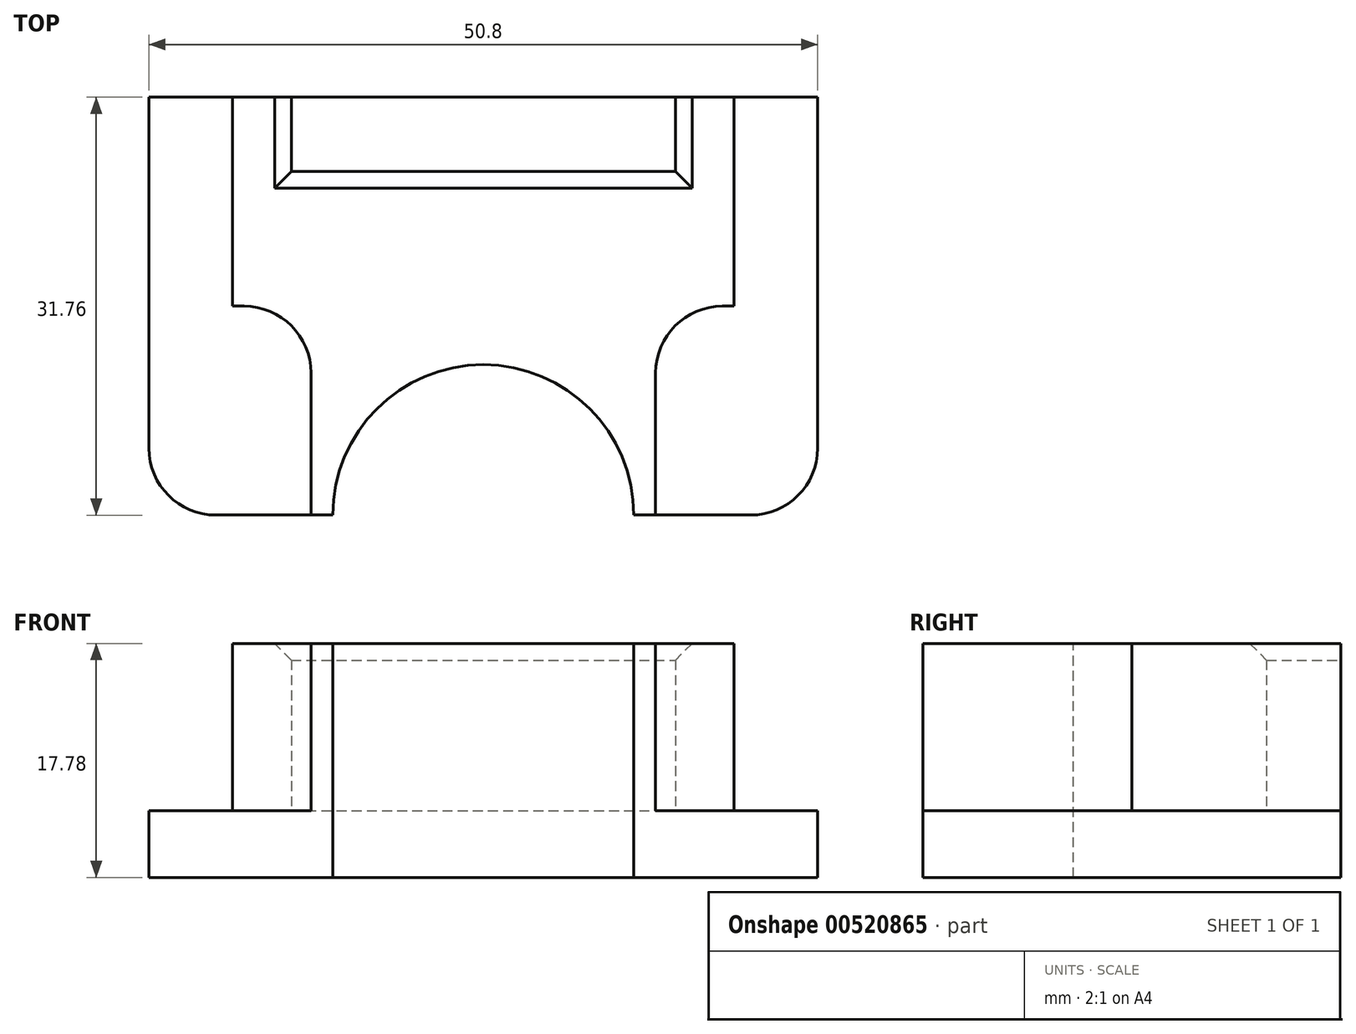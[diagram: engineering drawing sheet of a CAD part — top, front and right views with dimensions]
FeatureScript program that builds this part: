
annotation { "Feature Type Name" : "Feature", "Feature Type Description" : "" }
export const myFeature = defineFeature(function(context is Context, id is Id, definition is map)
    precondition{}
    {
        {
            var Q0;
            Q0=qCreatedBy(makeId("Top.planeOp"),FACE);
            var sketch = newSketch(context, id + "F0", { "sketchPlane" : qUnion([Q0])});
            skLineSegment(sketch, "E0.bottom", {"start": v(-25.4, 15.87) * mm, "end": v(25.4, 15.87) * mm});
            skLineSegment(sketch, "E0.top", {"start": v(-25.4, -15.88) * mm, "end": v(25.4, -15.88) * mm});
            skLineSegment(sketch, "E0.left", {"start": v(-25.4, 15.87) * mm, "end": v(-25.4, -15.88) * mm});
            skLineSegment(sketch, "E0.right", {"start": v(25.4, 15.87) * mm, "end": v(25.4, -15.88) * mm});
            skPoint(sketch, "E0.middle", {"position": v(0, 0) * mm});
            skSolve(sketch);
        }
        {
            var Q0;
            Q0=makeQuery(id+"F0.imprint","IMPRINT",FACE,{"disambiguationData":[TD([[makeQuery(id+"F0.imprint","IMPRINT",EDGE,{"derivedFrom":sQuery(id+"F0.wireOp",EDGE,"E0.bottom")}),-1.0]])]});
            extrude(context, id + "F1", {"entities" : qUnion([Q0]), "depth" : 5.08 * mm, "offsetDistance" : 25.4 * mm});
        }
        {
            var Q0;
            Q0=makeQuery(id+"F1.opExtrude","CAP_FACE",FACE,{"disambiguationData":[OSD([sQuery(id+"F0.wireOp",EDGE,"E0.bottom"),sQuery(id+"F0.wireOp",EDGE,"E0.top"),sQuery(id+"F0.wireOp",EDGE,"E0.left"),sQuery(id+"F0.wireOp",EDGE,"E0.right")])],"isStart":false});
            var sketch = newSketch(context, id + "F2", { "sketchPlane" : qUnion([Q0])});
            skLineSegment(sketch, "E1", {"start": v(-19.05, 15.87) * mm, "end": v(-19.05, 0) * mm});
            skLineSegment(sketch, "E2", {"start": v(-19.05, 0) * mm, "end": v(-13.1, 0) * mm});
            skLineSegment(sketch, "E3", {"start": v(-13.1, 0) * mm, "end": v(-13.1, -15.88) * mm});
            skLineSegment(sketch, "E4", {"start": v(-13.1, -15.88) * mm, "end": v(13.1, -15.88) * mm});
            skLineSegment(sketch, "E5", {"start": v(13.1, -15.88) * mm, "end": v(13.1, 0) * mm});
            skLineSegment(sketch, "E6", {"start": v(13.1, 0) * mm, "end": v(19.05, 0) * mm});
            skLineSegment(sketch, "E7", {"start": v(19.05, 0) * mm, "end": v(19.05, 15.87) * mm});
            skLineSegment(sketch, "E8", {"start": v(-19.05, 15.87) * mm, "end": v(-14.6, 15.87) * mm});
            skLineSegment(sketch, "E9", {"start": v(-14.6, 15.87) * mm, "end": v(-14.6, 10.23) * mm});
            skLineSegment(sketch, "E10", {"start": v(-14.6, 10.23) * mm, "end": v(14.6, 10.23) * mm});
            skLineSegment(sketch, "E11", {"start": v(14.6, 10.23) * mm, "end": v(14.6, 15.87) * mm});
            skLineSegment(sketch, "E12", {"start": v(14.6, 15.87) * mm, "end": v(19.05, 15.87) * mm});
            skLineSegment(sketch, "E13", {"start": v(0, 15.87) * mm, "end": v(0, -15.88) * mm, "construction": true});
            skSolve(sketch);
        }
        {
            var Q0;
            Q0=makeQuery(id+"F2.imprint","IMPRINT",FACE,{"disambiguationData":[TD([[makeQuery(id+"F2.imprint","IMPRINT",EDGE,{"derivedFrom":sQuery(id+"F2.wireOp",EDGE,"E1")}),1.0]])]});
            extrude(context, id + "F3", {"entities" : qUnion([Q0]), "operationType" : NewBodyOperationType.ADD, "depth" : 12.7 * mm, "offsetDistance" : 25.4 * mm});
        }
        {
            var Q0;
            Q0=makeQuery(id+"F3.opExtrude","CAP_FACE",FACE,{"disambiguationData":[OSD([sQuery(id+"F2.wireOp",EDGE,"E1"),sQuery(id+"F2.wireOp",EDGE,"E2"),sQuery(id+"F2.wireOp",EDGE,"E3"),sQuery(id+"F2.wireOp",EDGE,"E4"),sQuery(id+"F2.wireOp",EDGE,"E5"),sQuery(id+"F2.wireOp",EDGE,"E6"),sQuery(id+"F2.wireOp",EDGE,"E7"),sQuery(id+"F2.wireOp",EDGE,"E8"),sQuery(id+"F2.wireOp",EDGE,"E9"),sQuery(id+"F2.wireOp",EDGE,"E10"),sQuery(id+"F2.wireOp",EDGE,"E11"),sQuery(id+"F2.wireOp",EDGE,"E12")])],"isStart":false});
            var sketch = newSketch(context, id + "F4", { "sketchPlane" : qUnion([Q0])});
            skCircle(sketch, "E14", {"center": v(0, -15.88) * mm, "radius": 11.43 * mm});
            skSolve(sketch);
        }
        {
            var Q0;
            {var subQ0=sQuery(id+"F4.wireOp",EDGE,"E14");var subQ1=makeQuery(id+"F3.opExtrude","CAP_EDGE",EDGE,{"disambiguationData":[OSD([sQuery(id+"F2.wireOp",EDGE,"E4")])],"isStart":false});var subQ2=makeQuery(id+"F4.imprint","INTERSECT",VERTEX,{"disambiguationData":[OD(0.0)],"derivedFrom":[subQ1,subQ0]});Q0=makeQuery(id+"F4.imprint","IMPRINT",FACE,{"disambiguationData":[TD([[makeQuery(id+"F4.imprint","IMPRINT",EDGE,{"disambiguationData":[TD([[subQ2,1.0]])],"derivedFrom":subQ0}),1.0]])]});}
            var Q1;
            Q1=makeQuery(id+"F1.opExtrude","CAP_FACE",FACE,{"disambiguationData":[OSD([sQuery(id+"F0.wireOp",EDGE,"E0.bottom"),sQuery(id+"F0.wireOp",EDGE,"E0.top"),sQuery(id+"F0.wireOp",EDGE,"E0.left"),sQuery(id+"F0.wireOp",EDGE,"E0.right")])],"isStart":true});
            extrude(context, id + "F5", {"entities" : qUnion([Q0]), "operationType" : NewBodyOperationType.REMOVE, "endBound" : BoundingType.UP_TO_SURFACE, "oppositeDirection" : true, "depth" : 25.4 * mm, "endBoundEntityFace" : qUnion([Q1]), "offsetDistance" : 25.4 * mm});
        }
        {
            var Q0;
            Q0=makeQuery(id+"F3.opExtrude","SWEPT_EDGE",EDGE,{"disambiguationData":[OSD([sQuery(id+"F2.wireOp",EDGE,"E2"),sQuery(id+"F2.wireOp",EDGE,"E3")])]});
            var Q1;
            Q1=makeQuery(id+"F3.opExtrude","SWEPT_EDGE",EDGE,{"disambiguationData":[OSD([sQuery(id+"F2.wireOp",EDGE,"E5"),sQuery(id+"F2.wireOp",EDGE,"E6")])]});
            fillet(context, id + "F6", {"entities" : qUnion([Q0, Q1]), "radius" : 5.08 * mm, "tangentPropagation" : true, "allowEdgeOverflow" : false});
        }
        {
            var Q0;
            Q0=makeQuery(id+"F1.opExtrude","SWEPT_EDGE",EDGE,{"disambiguationData":[OSD([sQuery(id+"F0.wireOp",EDGE,"E0.top"),sQuery(id+"F0.wireOp",EDGE,"E0.right")])]});
            var Q1;
            Q1=makeQuery(id+"F1.opExtrude","SWEPT_EDGE",EDGE,{"disambiguationData":[OSD([sQuery(id+"F0.wireOp",EDGE,"E0.top"),sQuery(id+"F0.wireOp",EDGE,"E0.left")])]});
            fillet(context, id + "F7", {"entities" : qUnion([Q0, Q1]), "radius" : 5.08 * mm, "tangentPropagation" : true, "allowEdgeOverflow" : false});
        }
        {
            var Q0;
            Q0=makeQuery(id+"F5.boolean.opBoolean","COPY",EDGE,{"derivedFrom":makeQuery(id+"F5.opExtrude","CAP_EDGE",EDGE,{"disambiguationData":[OSD([sQuery(id+"F4.wireOp",EDGE,"E14")])],"isStart":true})});
            var Q1;
            Q1=makeQuery(id+"F3.opExtrude","CAP_EDGE",EDGE,{"disambiguationData":[OSD([sQuery(id+"F2.wireOp",EDGE,"E10")])],"isStart":false});
            var Q2;
            Q2=makeQuery(id+"F3.opExtrude","CAP_EDGE",EDGE,{"disambiguationData":[OSD([sQuery(id+"F2.wireOp",EDGE,"E9")])],"isStart":false});
            var Q3;
            Q3=makeQuery(id+"F3.opExtrude","CAP_EDGE",EDGE,{"disambiguationData":[OSD([sQuery(id+"F2.wireOp",EDGE,"E11")])],"isStart":false});
            chamfer(context, id + "F8", {"entities" : qUnion([Q0, Q1, Q2, Q3]), "width" : 1.27 * mm, "tangentPropagation" : true});
        }
    });
